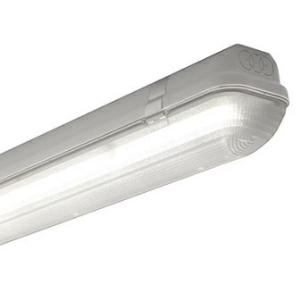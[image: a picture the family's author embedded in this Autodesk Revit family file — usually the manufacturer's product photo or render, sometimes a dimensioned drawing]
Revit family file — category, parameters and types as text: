
# Revit family: 3f_filippi_-_3f_linda_3f_filippi_-_58561_-_3f_linda_led_1x12w_l660
name_source: partatom
category: Lighting Fixtures
units: mm (PartAtom-declared; Revit-internal decimal feet)

## family parameters
Cut with Voids When Loaded = No
Host = Face
Light Source = No
Part Type = Normal
Room Calculation Point = No
Round Connector Dimension = Use Diameter
Shared = No

## types (1)
- 3F Filippi - 3F Linda (1 x LED, 2033 lm, 14 W, 4000 K)
    Apparent Load = 14 VA
    Approval mark = CE
    CIE Flux Codes = 44 77 94 97 100
    Color Rendering = 80
    Color Temperature = 4000 K
    Control Gear = Electronic ballast
    Default Elevation = 1800 mm
    Description = ILLUMINOTECHNICAL
Luminous efficiency 100% (DLOR 97%, ULOR 3%).
Initial luminous flux of the luminaire 2033 lm.
Controlled symmetric distribution.
Installation Interdistance Transv.D = 1.77 x hu - Long.D = 1.17 x hu.
Tabular UGR (CIE 117 - 4H-8H; S=0.25H; 70/50/20): RUG 21.8 - 22.6.
Beam angle: 109° - 64°.
Luminous efficacy 145 lm/W.
Lifetime (L93/B10): 30000 h. (tq+25°C)
Lifetime (L90/B10): 50000 h. (tq+25°C)
Lifetime (L85/B10): 80000 h. (tq+25°C)
Lifetime (L80/B10): 100000 h. (tq+25°C)
Lifetime (L85/B10): 50000 h. (tq+35°C)
Sudden decreased luminous flux after 50000 hours: 0% (C0).
Photobiological safety in compliance with IEC/TR 62778: RG0 risk exempt, (IEC 62471).
In compliance with IEC/EN 62722-2-1 - IEC/EN 62717 standards.

SOURCE
Linear LED module 12W/840.
Energy efficiency class (UE 2019/2020 - UE 2019/2015): D.
CIE 13.3 Colour rendering index: CRI >80 (R9 <50%).
IES TM-30 Fidelity Index: Rf = 84 Rg = 95.
CCT nominal colour temperature 4000 K.
Colour initial tolerance (MacAdam): SDCM 3.

MECHANICAL
Self-extinguishing V2 polycarbonate housing, injection moulded, RAL 7035 grey.
Ecologic anti-aging injected sealing gasket.
Diffuser in self-extinguishing V2 polycarbonate, photo-engraved interior, UV stabilised, injection moulded with smooth outer surface, tamper-proof opening.
Gear-holder reflector in hot-dip galvanised steel, painted with white polyester base.
Snug fit safety snap-lock clips for diffuser mounting in stainless steel, screwdriver opening.
Fixing brackets in stainless steel.
Possibility for technicians to access the interior of the luminaire.
Luminaire with limited surface temperature. - D - (EN 60598-2-24)
Dimensions: 660x100 mm, height 100 mm. Weight 1 kg.
IP66 protection degree.
Mechanical strength to impacts IK10 (20 joule).
Glow-wire test resistance 850°C.

ELECTRICAL
Halogen Free electronic wiring 230V-50/60Hz, power factor 0.95, THD <25%, constant output current, SELV, class I, 1 driver.
Power of the luminaire 14 W.
ENEC - CE.
SAFE FLICKER: PstLM=<1 and SVM=<0.4 (IEC TR 61547-1 and IEC TR 63158), to ensure a more comfortable and safe light.
Luminaire compliant with EN 60598-2-22 for power supply from a centralised emergency system CPSS (Central Power Supply System), not incorporated in the luminaire - high risk areas excluded. The default power and flux are 100% in AC and 100% in DC.
Ambient temperature from -20°C to +35°C.
Temperature class T6 max 85°C.
Relative humidity UR: <85%.

INSTALLATION
Ceiling / Suspended / Wall.
All accessories dedicated to this product are available on the Catalog and on our website www.3F-Filippi.com.

APPLICATIONS
Suitable product for food production plants (HACCP), IFS (Food Version 6), BRC (GSFS Food Version 7).
Dry, dusty indoor environments, subject to occasional water splashes.
Virtually shatterproof polycarbonate compatibly with the fumes / atmospheres that compromise the elasticity of plastic materials.
Not suitable for installation on surfaces subject to important vibrations, exposed to weather conditions, on ropes or poles.
Suitable for illumination of public car parks and parking grounds referred to DIN 67528:2018-04.

WARNING
Fixture not suitable for cold stores with an ambient temperature <0°C and/or relative humidity >85%.
Luminaire designed for disposal/recycling at end-of-life.
Replaceable (LED only) light source by a professional. Replaceable control gear by a professional.
    Height = 100 mm  [stored 0.328084 ft]
    Lamp = 1 x LED
    Lamp Light Flux = 2033 lm
    Lamp Power = 14 W
    Lamp count = 1
    Length = 660 mm
    Lifetime = 50000 h
    Luminous efficacy = 145 lm/W
    Manufacturer = 3F Filippi
    ModVariant = No
    Model = 3F Filippi - 58561 - 3F Linda LED 1x12W L660
    Mounting Place = Ceiling
    Mounting Type = Pendant
    Number of Poles = 1
    OnlyDefault = Yes
    Power Factor = 1
    Product Name = 3F Filippi - 3F Linda
    Product group = pendant luminaire
    ProductGroupID = 9
    Protection Class = Protection class I
    Protection Degree = IP 66
    RLX_Detail_Level = 1
    RLX_Emergency_Light_Flux = 0 lm
    RLX_Emergency_Type = 0
    RLX_Emergency_Type_DB = No
    RlxData = <blob elided: 68801 chars, md5=83d5e720>
    Socket = socket
    Standby Power = 0 W
    System Light Flux = 2033 lm
    System Power = 14 W
    Type Comments = Product without accessories
    Type Image = 3ffilippi_58561.jpg
    URL = http://relux.com
    VarID = ---
    Voltage = 0 V
    Weight = 0.00 kg
    Width = 100 mm  [stored 0.328084 ft]

note: [stored X ft] marks values corroborated as IEEE doubles in the binary element streams (Revit-internal decimal feet)

## geometry (parser evidence)
native form markers: Blend x4, Sweep x8
no freeform markers — native parametric forms only
